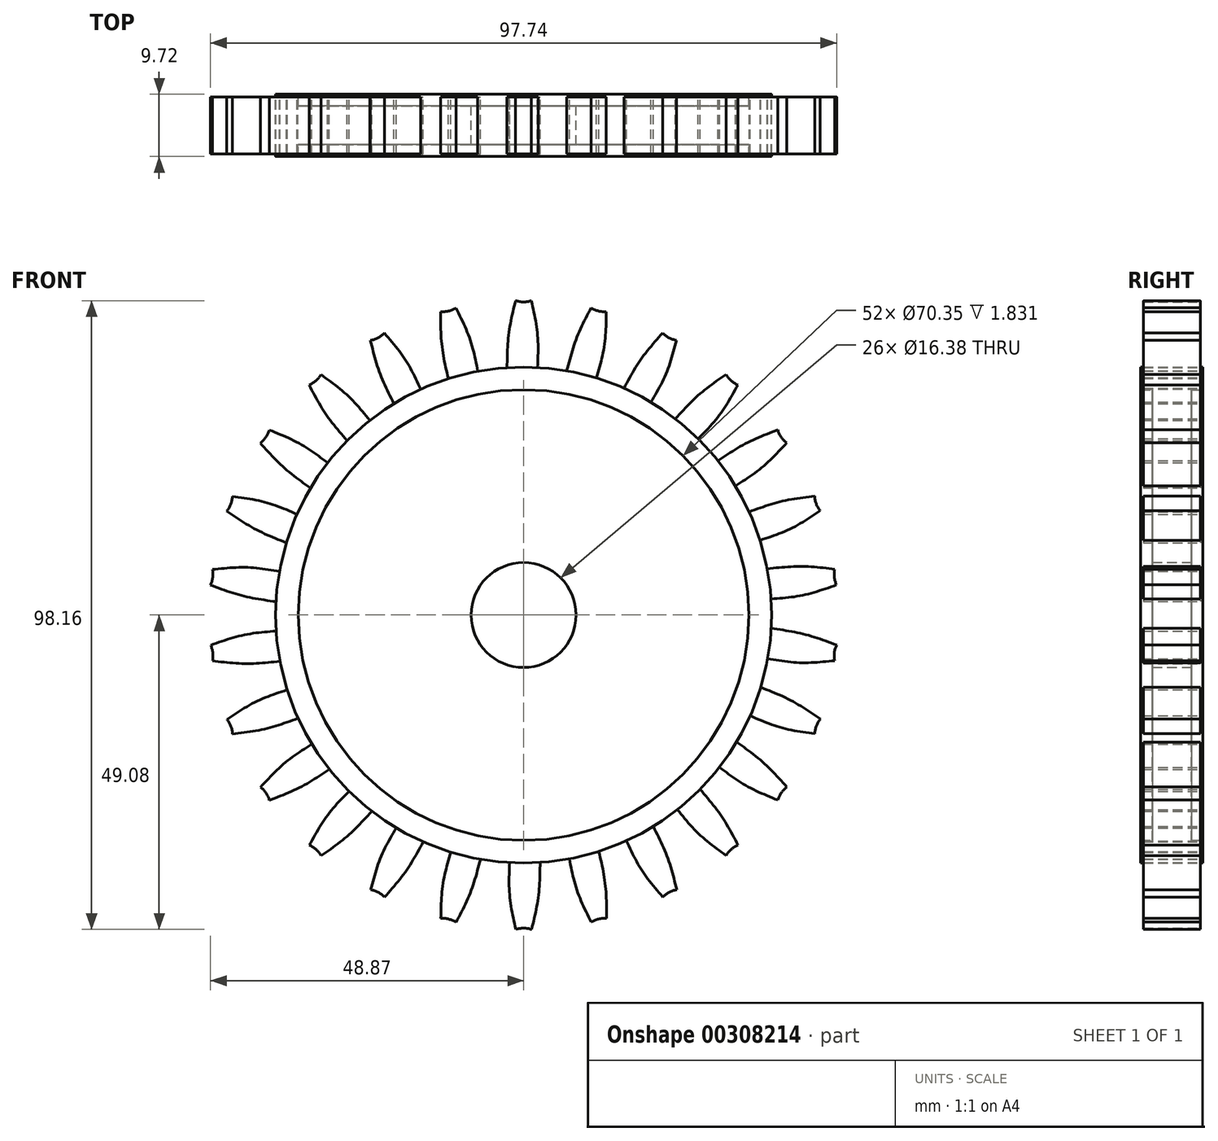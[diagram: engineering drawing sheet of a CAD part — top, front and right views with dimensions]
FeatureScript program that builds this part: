
annotation { "Feature Type Name" : "Feature", "Feature Type Description" : "" }
export const myFeature = defineFeature(function(context is Context, id is Id, definition is map)
    precondition{}
    {
        {
            var Q0;
            Q0=qCreatedBy(makeId("Front.planeOp"),FACE);
            var sketch = newSketch(context, id + "F0", { "sketchPlane" : qUnion([Q0])});
            skCircle(sketch, "E0", {"center": v(0, 0) * mm, "radius": 38.73 * mm});
            skCircle(sketch, "E1", {"center": v(0, 0) * mm, "radius": 35.18 * mm});
            skCircle(sketch, "E2", {"center": v(0, 0) * mm, "radius": 8.2 * mm});
            skArc(sketch, "E3", {"start": v(-1.25, 49.08) * mm, "mid": v(-0.02, 48.88) * mm, "end": v(1.22, 49.07) * mm});
            skFitSpline(sketch, "E4", {"points": [v(-1.25, 49.08) * mm, v(-2.31, 43.9) * mm, v(-2.58, 38.64) * mm], "startDerivative": vector(-2.41, -10) * mm, "endDerivative": vector(-0.14, -10.58) * mm});
            skPoint(sketch, "E5.1.internal.snap0", {"position": v(2.17, 45.67) * mm});
            skPoint(sketch, "E5.2.internal.snap0", {"position": v(2.17, 45.67) * mm});
            skFitSpline(sketch, "E5", {"points": [v(1.22, 49.07) * mm, v(2.17, 43.82) * mm, v(2.17, 38.67) * mm], "startDerivative": vector(2.26, -10.12) * mm, "endDerivative": vector(-0.45, -10.34) * mm});
            skPoint(sketch, "E6.orphan", {"position": v(4.35, 38.48) * mm});
            skSolve(sketch);
        }
        {
            var Q0;
            Q0=makeQuery(id+"F0.imprint","IMPRINT",FACE,{"disambiguationData":[TD([[makeQuery(id+"F0.imprint","IMPRINT",EDGE,{"derivedFrom":sQuery(id+"F0.wireOp",EDGE,"E1")}),1.0]])]});
            extrude(context, id + "F1", {"entities" : qUnion([Q0]), "endBound" : BoundingType.SYMMETRIC, "depth" : 6.05 * mm});
        }
        {
            var Q0;
            Q0=makeQuery(id+"F0.imprint","IMPRINT",FACE,{"disambiguationData":[TD([[makeQuery(id+"F0.imprint","IMPRINT",EDGE,{"derivedFrom":sQuery(id+"F0.wireOp",EDGE,"E1")}),-1.0]])]});
            extrude(context, id + "F2", {"entities" : qUnion([Q0]), "operationType" : NewBodyOperationType.ADD, "endBound" : BoundingType.SYMMETRIC, "depth" : 9.71 * mm});
        }
        {
            var Q0;
            Q0=makeQuery(id+"F0.imprint","IMPRINT",FACE,{"disambiguationData":[TD([[makeQuery(id+"F0.imprint","IMPRINT",EDGE,{"derivedFrom":sQuery(id+"F0.wireOp",EDGE,"E3")}),-1.0]])]});
            extrude(context, id + "F3", {"entities" : qUnion([Q0]), "operationType" : NewBodyOperationType.ADD, "endBound" : BoundingType.SYMMETRIC, "depth" : 8.87 * mm});
        }
        {
            var Q0;
            Q0=makeQuery(id+"F1.opExtrude","SWEPT_BODY",BODY,{"disambiguationData":[OSD([sQuery(id+"F0.wireOp",EDGE,"E1"),sQuery(id+"F0.wireOp",EDGE,"E2")])]});
            var Q1;
            Q1=makeQuery(id+"F1.opExtrude","SWEPT_FACE",FACE,{"disambiguationData":[OSD([sQuery(id+"F0.wireOp",EDGE,"E2")])]});
            circularPattern(context, id + "F4", {"entities" : qUnion([Q0]), "axis" : qUnion([Q1]), "angle" : 360 * degree, "instanceCount" : 26, "equalSpace" : true});
        }
    });
